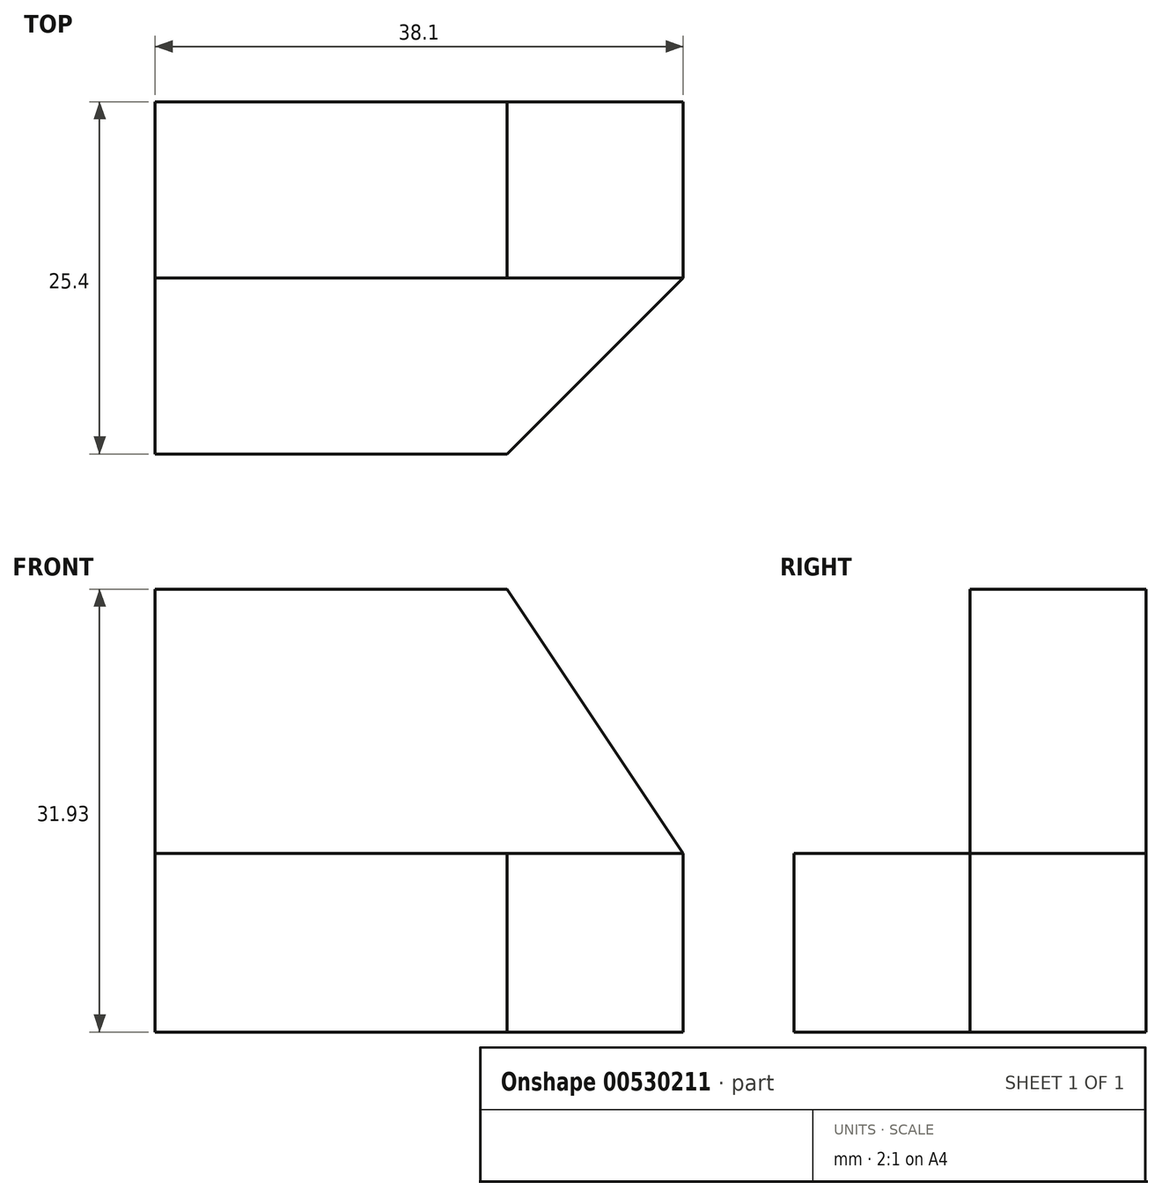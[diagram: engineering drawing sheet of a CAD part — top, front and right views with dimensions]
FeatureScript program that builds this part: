
annotation { "Feature Type Name" : "Feature", "Feature Type Description" : "" }
export const myFeature = defineFeature(function(context is Context, id is Id, definition is map)
    precondition{}
    {
        {
            var Q0;
            Q0=qCreatedBy(makeId("Front.planeOp"),FACE);
            var sketch = newSketch(context, id + "F0", { "sketchPlane" : qUnion([Q0])});
            skLineSegment(sketch, "E0", {"start": v(-44.95, 0) * mm, "end": v(-6.85, 0) * mm});
            skLineSegment(sketch, "E1", {"start": v(-6.85, 0) * mm, "end": v(-6.85, 12.88) * mm});
            skLineSegment(sketch, "E2", {"start": v(-6.85, 12.88) * mm, "end": v(-44.95, 12.88) * mm});
            skLineSegment(sketch, "E3", {"start": v(-44.95, 12.88) * mm, "end": v(-44.95, 0) * mm});
            skSolve(sketch);
        }
        {
            var Q0;
            Q0=makeQuery(id+"F0.imprint","IMPRINT",FACE,{"disambiguationData":[TD([[makeQuery(id+"F0.imprint","IMPRINT",EDGE,{"derivedFrom":sQuery(id+"F0.wireOp",EDGE,"E0")}),1.0]])]});
            extrude(context, id + "F1", {"entities" : qUnion([Q0]), "depth" : 25.4 * mm, "offsetDistance" : 25.4 * mm});
        }
        {
            var Q0;
            Q0=makeQuery(id+"F1.opExtrude","SWEPT_FACE",FACE,{"disambiguationData":[OSD([sQuery(id+"F0.wireOp",EDGE,"E2")])]});
            var sketch = newSketch(context, id + "F2", { "sketchPlane" : qUnion([Q0])});
            skLineSegment(sketch, "E4", {"start": v(-6.85, -12.7) * mm, "end": v(-44.95, -12.7) * mm});
            skLineSegment(sketch, "E5", {"start": v(-44.95, -12.7) * mm, "end": v(-44.95, 0) * mm});
            skLineSegment(sketch, "E6", {"start": v(-44.95, 0) * mm, "end": v(-6.85, 0) * mm});
            skLineSegment(sketch, "E7", {"start": v(-6.85, 0) * mm, "end": v(-6.85, -12.7) * mm});
            skSolve(sketch);
        }
        {
            var Q0;
            Q0 = qSketchRegion(id + "F2", true);
            extrude(context, id + "F3", {"entities" : qUnion([Q0]), "operationType" : NewBodyOperationType.ADD, "depth" : 19.05 * mm, "offsetDistance" : 25.4 * mm});
        }
        {
            var Q0;
            Q0=makeQuery(id+"F1.opExtrude","SWEPT_FACE",FACE,{"disambiguationData":[OSD([sQuery(id+"F0.wireOp",EDGE,"E2")])]});
            var sketch = newSketch(context, id + "F4", { "sketchPlane" : qUnion([Q0])});
            skLineSegment(sketch, "E8", {"start": v(-6.85, -12.7) * mm, "end": v(-19.55, -25.4) * mm});
            skSolve(sketch);
        }
        {
            var Q0;
            {var subQ0=sQuery(id+"F4.wireOp",EDGE,"E8");Q0=makeQuery(id+"F4.imprint","IMPRINT",FACE,{"disambiguationData":[TD([[makeQuery(id+"F4.imprint","IMPRINT",EDGE,{"derivedFrom":subQ0}),1.0]])]});}
            extrude(context, id + "F5", {"entities" : qUnion([Q0]), "operationType" : NewBodyOperationType.REMOVE, "endBound" : BoundingType.THROUGH_ALL, "oppositeDirection" : true, "depth" : 25.4 * mm, "offsetDistance" : 25.4 * mm});
        }
        {
            var Q0;
            Q0=makeQuery(id+"F3.opExtrude","SWEPT_FACE",FACE,{"disambiguationData":[OSD([sQuery(id+"F2.wireOp",EDGE,"E4")])]});
            var sketch = newSketch(context, id + "F6", { "sketchPlane" : qUnion([Q0])});
            skLineSegment(sketch, "E9", {"start": v(-6.85, 12.88) * mm, "end": v(-19.55, 31.93) * mm});
            skSolve(sketch);
        }
        {
            var Q0;
            {var subQ0=sQuery(id+"F6.wireOp",EDGE,"E9");Q0=makeQuery(id+"F6.imprint","IMPRINT",FACE,{"disambiguationData":[TD([[makeQuery(id+"F6.imprint","IMPRINT",EDGE,{"derivedFrom":subQ0}),-1.0]])]});}
            extrude(context, id + "F7", {"entities" : qUnion([Q0]), "operationType" : NewBodyOperationType.REMOVE, "endBound" : BoundingType.THROUGH_ALL, "oppositeDirection" : true, "depth" : 25.4 * mm, "offsetDistance" : 25.4 * mm});
        }
    });
